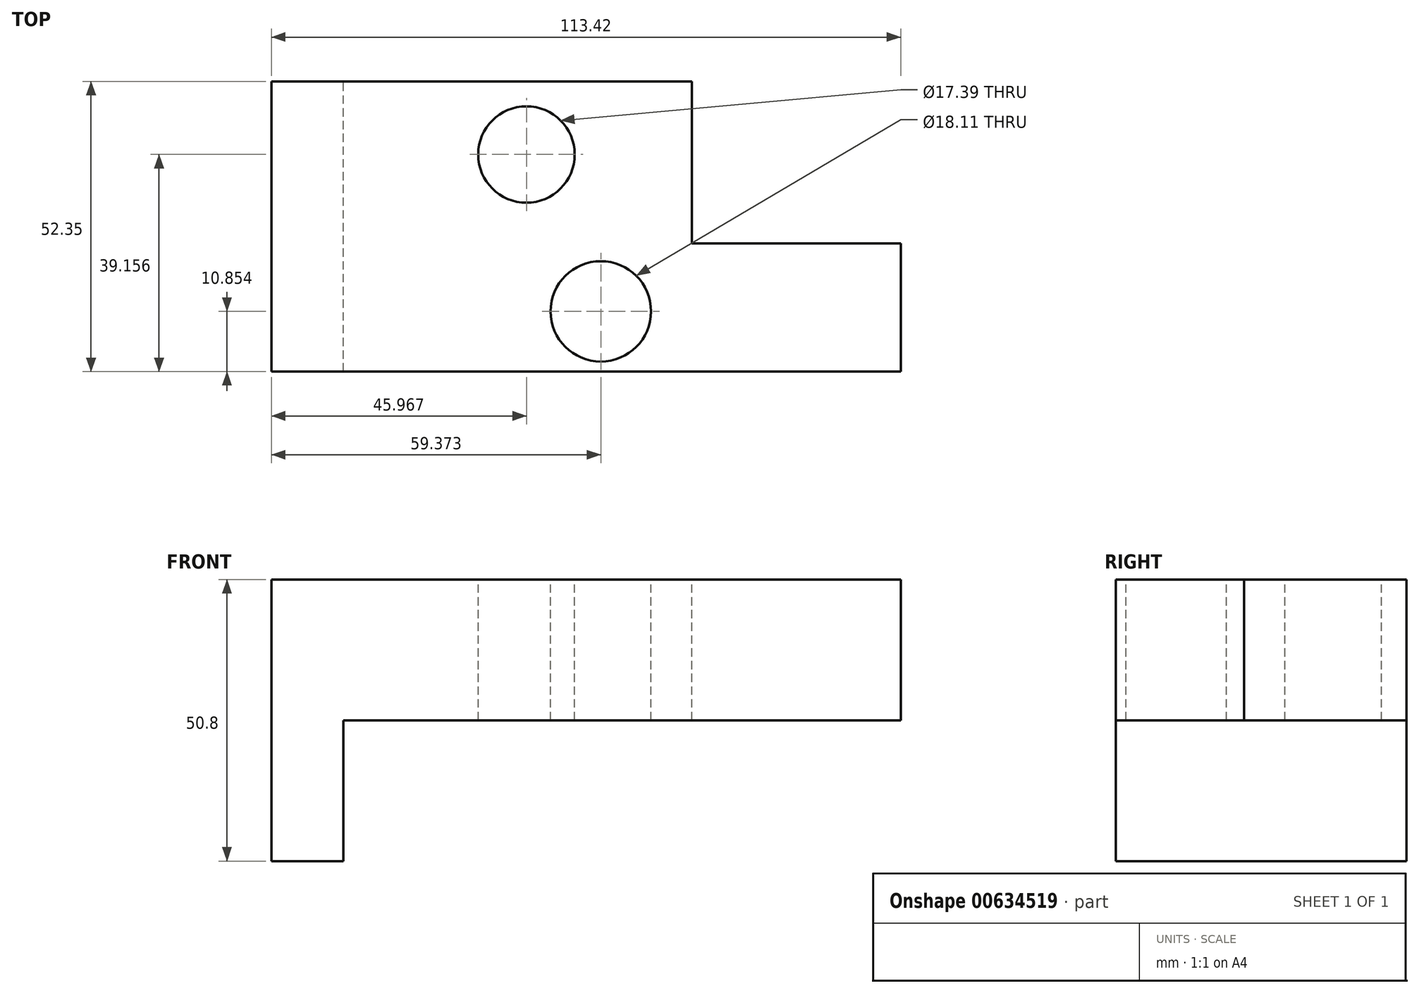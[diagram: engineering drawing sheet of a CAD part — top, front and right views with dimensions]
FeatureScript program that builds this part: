
annotation { "Feature Type Name" : "Feature", "Feature Type Description" : "" }
export const myFeature = defineFeature(function(context is Context, id is Id, definition is map)
    precondition{}
    {
        {
            var Q0;
            Q0=qCreatedBy(makeId("Top.planeOp"),FACE);
            var sketch = newSketch(context, id + "F0", { "sketchPlane" : qUnion([Q0])});
            skLineSegment(sketch, "E0.bottom", {"start": v(-48.84, 29.26) * mm, "end": v(26.92, 29.26) * mm});
            skLineSegment(sketch, "E0.top", {"start": v(-48.84, -23.09) * mm, "end": v(26.92, -23.09) * mm});
            skLineSegment(sketch, "E0.left", {"start": v(-48.84, 29.26) * mm, "end": v(-48.84, -23.09) * mm});
            skLineSegment(sketch, "E1.bottom", {"start": v(26.92, 0) * mm, "end": v(64.58, 0) * mm});
            skLineSegment(sketch, "E1.top", {"start": v(26.92, -23.09) * mm, "end": v(64.58, -23.09) * mm});
            skLineSegment(sketch, "E1.right", {"start": v(64.58, 0) * mm, "end": v(64.58, -23.09) * mm});
            skLineSegment(sketch, "E2", {"start": v(26.92, 0) * mm, "end": v(26.92, 29.26) * mm});
            skCircle(sketch, "E3", {"center": v(-2.87, 16.07) * mm, "radius": 8.7 * mm});
            skCircle(sketch, "E4", {"center": v(10.53, -12.24) * mm, "radius": 9.05 * mm});
            skSolve(sketch);
        }
        {
            var Q0;
            Q0=makeQuery(id+"F0.imprint","IMPRINT",FACE,{"disambiguationData":[TD([[makeQuery(id+"F0.imprint","IMPRINT",EDGE,{"derivedFrom":sQuery(id+"F0.wireOp",EDGE,"E0.bottom")}),-1.0]])]});
            extrude(context, id + "F1", {"entities" : qUnion([Q0]), "oppositeDirection" : true, "depth" : 25.4 * mm, "offsetDistance" : 25.4 * mm});
        }
        {
            var Q0;
            Q0=makeQuery(id+"F1.opExtrude","CAP_FACE",FACE,{"disambiguationData":[OSD([sQuery(id+"F0.wireOp",EDGE,"E0.bottom"),sQuery(id+"F0.wireOp",EDGE,"E0.top"),sQuery(id+"F0.wireOp",EDGE,"E0.left"),sQuery(id+"F0.wireOp",EDGE,"E1.bottom"),sQuery(id+"F0.wireOp",EDGE,"E1.top"),sQuery(id+"F0.wireOp",EDGE,"E1.right"),sQuery(id+"F0.wireOp",EDGE,"E2"),sQuery(id+"F0.wireOp",EDGE,"E3"),sQuery(id+"F0.wireOp",EDGE,"E4")])],"isStart":false});
            var sketch = newSketch(context, id + "F2", { "sketchPlane" : qUnion([Q0])});
            skLineSegment(sketch, "E5.bottom", {"start": v(-48.84, 23.09) * mm, "end": v(-35.86, 23.09) * mm});
            skLineSegment(sketch, "E5.top", {"start": v(-48.84, -29.26) * mm, "end": v(-35.86, -29.26) * mm});
            skLineSegment(sketch, "E5.left", {"start": v(-48.84, 23.09) * mm, "end": v(-48.84, -29.26) * mm});
            skLineSegment(sketch, "E5.right", {"start": v(-35.86, 23.09) * mm, "end": v(-35.86, -29.26) * mm});
            skLineSegment(sketch, "E6.bottom", {"start": v(51.18, 23.09) * mm, "end": v(64.58, 23.09) * mm});
            skLineSegment(sketch, "E6.top", {"start": v(51.18, 0) * mm, "end": v(64.58, 0) * mm});
            skLineSegment(sketch, "E6.right", {"start": v(64.58, 23.09) * mm, "end": v(64.58, 0) * mm});
            skLineSegment(sketch, "E7.bottom", {"start": v(64.58, 23.09) * mm, "end": v(51.18, 23.09) * mm});
            skLineSegment(sketch, "E7.top", {"start": v(64.58, 0) * mm, "end": v(51.18, 0) * mm});
            skLineSegment(sketch, "E7.right", {"start": v(51.18, 23.09) * mm, "end": v(51.18, 0) * mm});
            skSolve(sketch);
        }
        {
            var Q0;
            Q0=makeQuery(id+"F2.imprint","IMPRINT",FACE,{"disambiguationData":[TD([[makeQuery(id+"F2.imprint","IMPRINT",EDGE,{"derivedFrom":sQuery(id+"F2.wireOp",EDGE,"E5.bottom")}),-1.0]])]});
            var Q1;
            Q1=makeQuery(id+"F2.imprint","IMPRINT",FACE,{"disambiguationData":[TD([[makeQuery(id+"F2.imprint","IMPRINT",EDGE,{"derivedFrom":sQuery(id+"F2.wireOp",EDGE,"E7.bottom")}),-1.0]])]});
            extrude(context, id + "F3", {"entities" : qUnion([Q0, Q1]), "operationType" : NewBodyOperationType.ADD, "depth" : 25.4 * mm, "offsetDistance" : 25.4 * mm});
        }
    });
